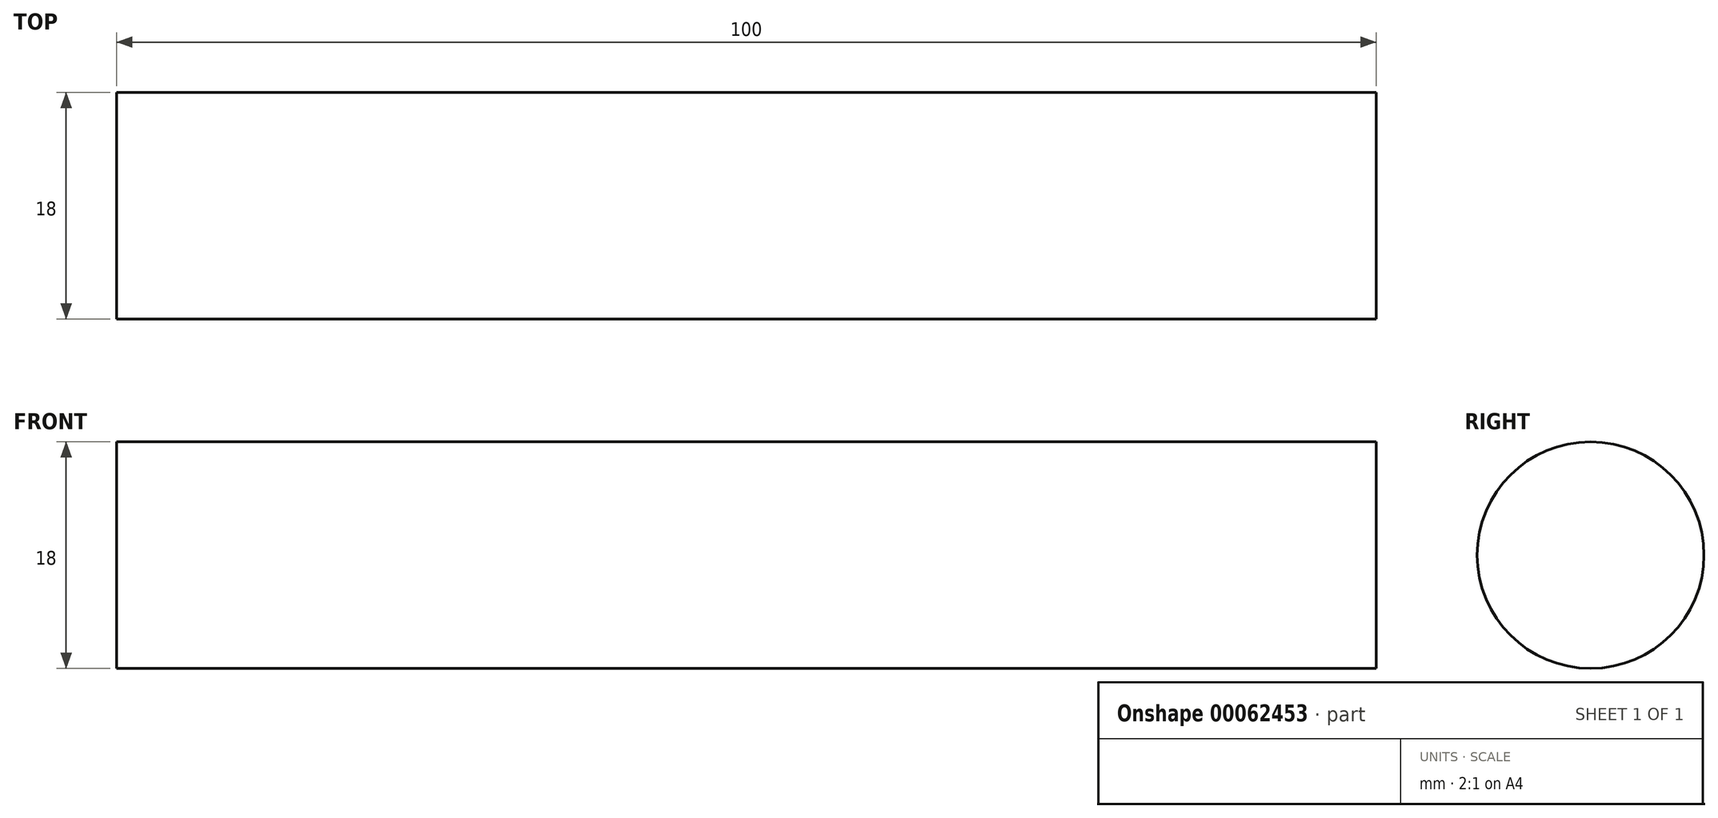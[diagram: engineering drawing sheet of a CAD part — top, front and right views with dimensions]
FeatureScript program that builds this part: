
annotation { "Feature Type Name" : "Feature", "Feature Type Description" : "" }
export const myFeature = defineFeature(function(context is Context, id is Id, definition is map)
    precondition{}
    {
        {
            var Q0;
            Q0=qCreatedBy(makeId("Right.planeOp"),FACE);
            var sketch = newSketch(context, id + "F0", { "sketchPlane" : qUnion([Q0])});
            skCircle(sketch, "E0", {"center": v(0, 0) * mm, "radius": 9 * mm});
            skSolve(sketch);
        }
        {
            var Q0;
            Q0 = qSketchRegion(id + "F0", true);
            extrude(context, id + "F1", {"entities" : qUnion([Q0]), "endBound" : BoundingType.SYMMETRIC, "depth" : 100 * mm});
        }
    });
